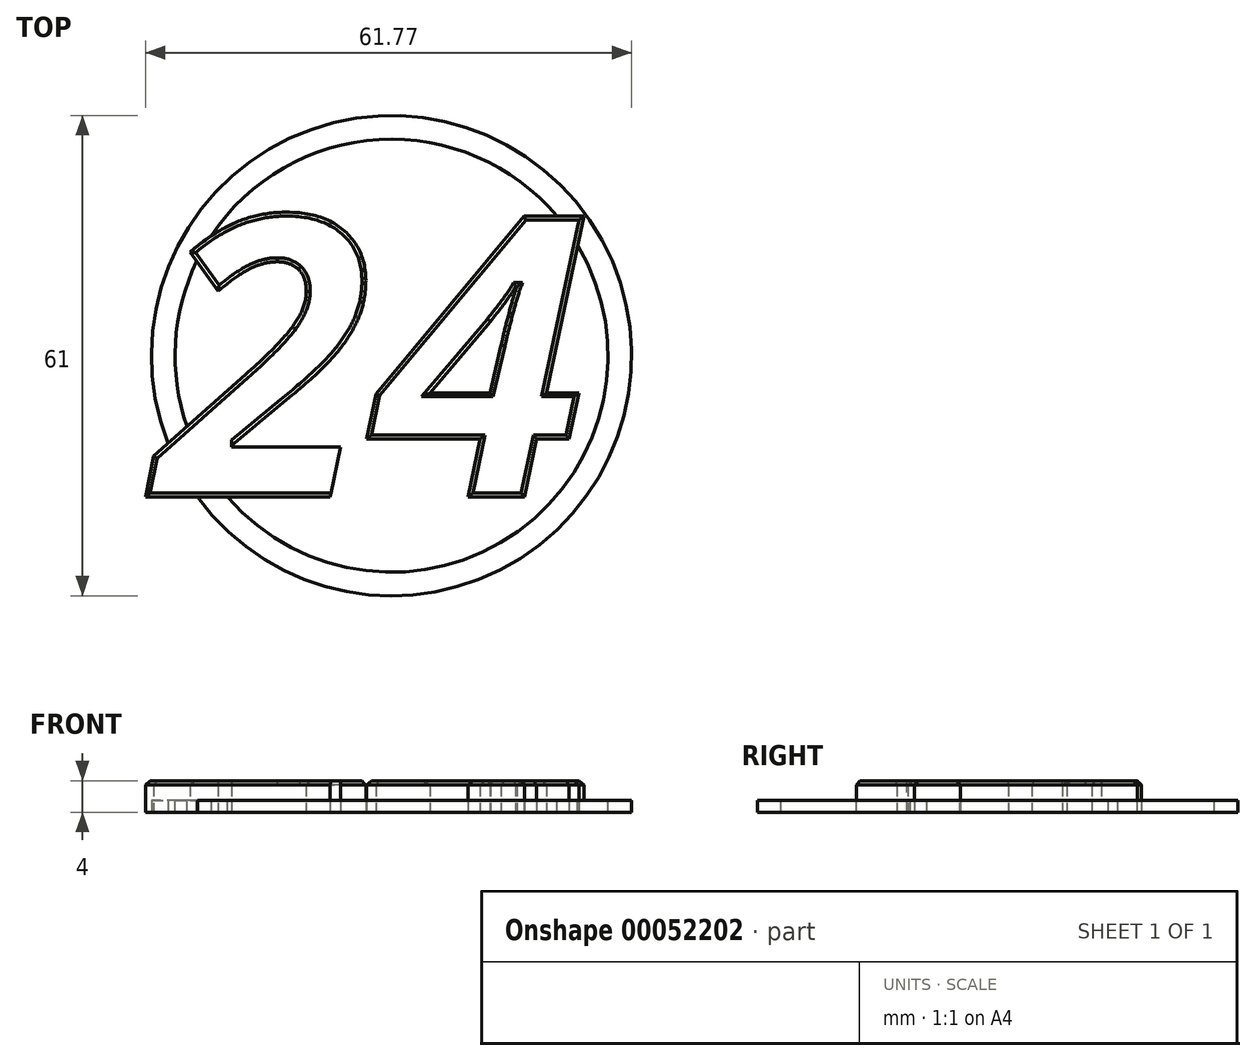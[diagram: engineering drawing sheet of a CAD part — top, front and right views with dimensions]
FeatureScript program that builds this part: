
annotation { "Feature Type Name" : "Feature", "Feature Type Description" : "" }
export const myFeature = defineFeature(function(context is Context, id is Id, definition is map)
    precondition{}
    {
        {
            var Q0;
            Q0=qCreatedBy(makeId("Top.planeOp"),FACE);
            var sketch = newSketch(context, id + "F0", { "sketchPlane" : qUnion([Q0])});
            skCircle(sketch, "E0", {"center": v(0, 0) * mm, "radius": 30.5 * mm});
            skSolve(sketch);
        }
        {
            var Q0;
            Q0=makeQuery(id+"F0.imprint","IMPRINT",FACE,{"disambiguationData":[TD([[makeQuery(id+"F0.imprint","IMPRINT",EDGE,{"derivedFrom":sQuery(id+"F0.wireOp",EDGE,"E0")}),1.0]])]});
            extrude(context, id + "F1", {"entities" : qUnion([Q0]), "depth" : 1.5 * mm});
        }
        {
            var Q0;
            Q0=makeQuery(id+"F1.opExtrude","CAP_FACE",FACE,{"disambiguationData":[OSD([sQuery(id+"F0.wireOp",EDGE,"E0")])],"isStart":false});
            var sketch = newSketch(context, id + "F2", { "sketchPlane" : qUnion([Q0])});
            skCircle(sketch, "E1", {"center": v(0, 0) * mm, "radius": 27.5 * mm});
            skSolve(sketch);
        }
        {
            var Q0;
            Q0=makeQuery(id+"F2.imprint","IMPRINT",FACE,{"disambiguationData":[TD([[makeQuery(id+"F2.imprint","IMPRINT",EDGE,{"derivedFrom":sQuery(id+"F2.wireOp",EDGE,"E1")}),1.0]])]});
            var Q1;
            Q1=makeQuery(id+"F1.opExtrude","CAP_FACE",FACE,{"disambiguationData":[OSD([sQuery(id+"F0.wireOp",EDGE,"E0")])],"isStart":true});
            extrude(context, id + "F3", {"entities" : qUnion([Q0]), "operationType" : NewBodyOperationType.REMOVE, "endBound" : BoundingType.THROUGH_ALL, "oppositeDirection" : true, "endBoundEntityFace" : qUnion([Q1]), "depth" : 3 * mm});
        }
        {
            var Q0;
            Q0=qCreatedBy(makeId("Top.planeOp"),FACE);
            var sketch = newSketch(context, id + "F4", { "sketchPlane" : qUnion([Q0])});
            skText(sketch, "E2", { "text": "24", "fontName": "OpenSans-BoldItalic.ttf"});
            const initialGuessF4  = {"E2": [-0.03007, -0.01797, 1, 0, 0.036]};
            skSetInitialGuess(sketch, initialGuessF4);
            skSolve(sketch);
        }
        {
            var Q0;
            Q0 = qSketchRegion(id + "F4", true);
            extrude(context, id + "F5", {"entities" : qUnion([Q0]), "operationType" : NewBodyOperationType.ADD, "depth" : 4 * mm});
        }
        {
            var Q0;
            Q0=makeQuery(id+"F5.opExtrude","CAP_EDGE",EDGE,{"disambiguationData":[OSD([sQuery(id+"F4.wireOp",EDGE,"E2.sketch_text.stroke-14")])],"isStart":false});
            var Q1;
            Q1=makeQuery(id+"F5.opExtrude","CAP_EDGE",EDGE,{"disambiguationData":[OSD([sQuery(id+"F4.wireOp",EDGE,"E2.sketch_text.stroke-15")])],"isStart":false});
            var Q2;
            Q2=makeQuery(id+"F5.opExtrude","CAP_EDGE",EDGE,{"disambiguationData":[OSD([sQuery(id+"F4.wireOp",EDGE,"E2.sketch_text.stroke-9")])],"isStart":false});
            var Q3;
            Q3=makeQuery(id+"F5.opExtrude","CAP_EDGE",EDGE,{"disambiguationData":[OSD([sQuery(id+"F4.wireOp",EDGE,"E2.sketch_text.stroke-10")])],"isStart":false});
            var Q4;
            Q4=makeQuery(id+"F5.opExtrude","CAP_EDGE",EDGE,{"disambiguationData":[OSD([sQuery(id+"F4.wireOp",EDGE,"E2.sketch_text.stroke-11")])],"isStart":false});
            var Q5;
            Q5=makeQuery(id+"F5.opExtrude","CAP_EDGE",EDGE,{"disambiguationData":[OSD([sQuery(id+"F4.wireOp",EDGE,"E2.sketch_text.stroke-12")])],"isStart":false});
            var Q6;
            Q6=makeQuery(id+"F5.opExtrude","CAP_EDGE",EDGE,{"disambiguationData":[OSD([sQuery(id+"F4.wireOp",EDGE,"E2.sketch_text.stroke-13")])],"isStart":false});
            var Q7;
            Q7=makeQuery(id+"F5.opExtrude","CAP_EDGE",EDGE,{"disambiguationData":[OSD([sQuery(id+"F4.wireOp",EDGE,"E2.sketch_text.stroke-8")])],"isStart":false});
            var Q8;
            Q8=makeQuery(id+"F5.opExtrude","CAP_EDGE",EDGE,{"disambiguationData":[OSD([sQuery(id+"F4.wireOp",EDGE,"E2.sketch_text.stroke-0")])],"isStart":false});
            var Q9;
            Q9=makeQuery(id+"F5.opExtrude","CAP_EDGE",EDGE,{"disambiguationData":[OSD([sQuery(id+"F4.wireOp",EDGE,"E2.sketch_text.stroke-1")])],"isStart":false});
            var Q10;
            Q10=makeQuery(id+"F5.opExtrude","CAP_EDGE",EDGE,{"disambiguationData":[OSD([sQuery(id+"F4.wireOp",EDGE,"E2.sketch_text.stroke-2")])],"isStart":false});
            var Q11;
            Q11=makeQuery(id+"F5.opExtrude","CAP_EDGE",EDGE,{"disambiguationData":[OSD([sQuery(id+"F4.wireOp",EDGE,"E2.sketch_text.stroke-4")])],"isStart":false});
            var Q12;
            Q12=makeQuery(id+"F5.opExtrude","CAP_EDGE",EDGE,{"disambiguationData":[OSD([sQuery(id+"F4.wireOp",EDGE,"E2.sketch_text.stroke-3")])],"isStart":false});
            var Q13;
            Q13=makeQuery(id+"F5.opExtrude","CAP_EDGE",EDGE,{"disambiguationData":[OSD([sQuery(id+"F4.wireOp",EDGE,"E2.sketch_text.stroke-5")])],"isStart":false});
            var Q14;
            Q14=makeQuery(id+"F5.opExtrude","CAP_EDGE",EDGE,{"disambiguationData":[OSD([sQuery(id+"F4.wireOp",EDGE,"E2.sketch_text.stroke-6")])],"isStart":false});
            var Q15;
            Q15=makeQuery(id+"F5.opExtrude","CAP_EDGE",EDGE,{"disambiguationData":[OSD([sQuery(id+"F4.wireOp",EDGE,"E2.sketch_text.stroke-7")])],"isStart":false});
            var Q16;
            Q16=makeQuery(id+"F5.opExtrude","CAP_FACE",FACE,{"disambiguationData":[OSD([sQuery(id+"F4.wireOp",EDGE,"E2.sketch_text.stroke-21"),sQuery(id+"F4.wireOp",EDGE,"E2.sketch_text.stroke-22"),sQuery(id+"F4.wireOp",EDGE,"E2.sketch_text.stroke-23"),sQuery(id+"F4.wireOp",EDGE,"E2.sketch_text.stroke-24"),sQuery(id+"F4.wireOp",EDGE,"E2.sketch_text.stroke-25"),sQuery(id+"F4.wireOp",EDGE,"E2.sketch_text.stroke-26"),sQuery(id+"F4.wireOp",EDGE,"E2.sketch_text.stroke-27"),sQuery(id+"F4.wireOp",EDGE,"E2.sketch_text.stroke-28"),sQuery(id+"F4.wireOp",EDGE,"E2.sketch_text.stroke-29"),sQuery(id+"F4.wireOp",EDGE,"E2.sketch_text.stroke-30"),sQuery(id+"F4.wireOp",EDGE,"E2.sketch_text.stroke-31"),sQuery(id+"F4.wireOp",EDGE,"E2.sketch_text.stroke-32"),sQuery(id+"F4.wireOp",EDGE,"E2.sketch_text.stroke-33"),sQuery(id+"F4.wireOp",EDGE,"E2.sketch_text.stroke-34"),sQuery(id+"F4.wireOp",EDGE,"E2.sketch_text.stroke-35"),sQuery(id+"F4.wireOp",EDGE,"E2.sketch_text.stroke-36"),sQuery(id+"F4.wireOp",EDGE,"E2.sketch_text.stroke-37"),sQuery(id+"F4.wireOp",EDGE,"E2.sketch_text.stroke-38")])],"isStart":false});
            chamfer(context, id + "F6", {"entities" : qUnion([Q0, Q1, Q2, Q3, Q4, Q5, Q6, Q7, Q8, Q9, Q10, Q11, Q12, Q13, Q14, Q15, Q16]), "width" : 0.5 * mm, "tangentPropagation" : true});
        }
    });
